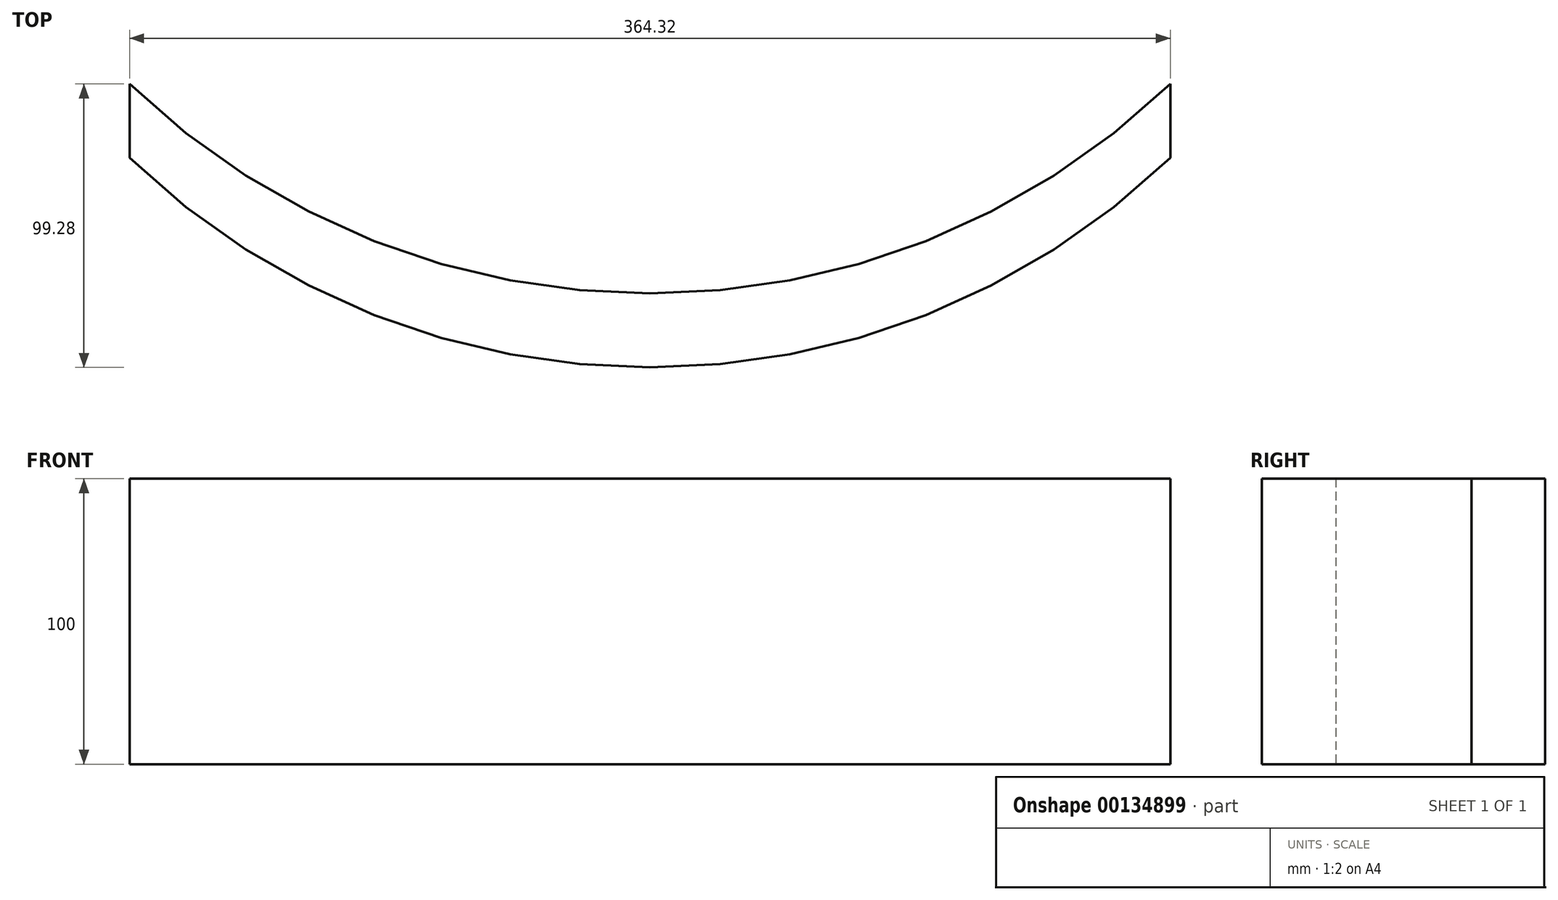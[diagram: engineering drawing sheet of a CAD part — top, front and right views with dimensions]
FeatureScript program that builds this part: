
annotation { "Feature Type Name" : "Feature", "Feature Type Description" : "" }
export const myFeature = defineFeature(function(context is Context, id is Id, definition is map)
    precondition{}
    {
        {
            var Q0;
            Q0=qCreatedBy(makeId("Top.planeOp"),FACE);
            var sketch = newSketch(context, id + "F0", { "sketchPlane" : qUnion([Q0])});
            skArc(sketch, "E0", {"start": v(-182.16, -189.43) * mm, "mid": v(0, -262.8) * mm, "end": v(182.16, -189.43) * mm});
            skLineSegment(sketch, "E1", {"start": v(-182.16, -189.43) * mm, "end": v(182.16, -189.43) * mm, "construction": true});
            skSolve(sketch);
        }
        {
            var Q0;
            Q0 = qSketchRegion(id + "F0", true);
            var Q1;
            Q1=sQuery(id+"F0.wireOp",EDGE,"E0");
            extrude(context, id + "F1", {"entities" : qUnion([Q0]), "bodyType" : ToolBodyType.SURFACE, "surfaceEntities" : qUnion([Q1]), "oppositeDirection" : true, "depth" : 100 * mm});
        }
        {
            var Q0;
            Q0=makeQuery(id+"F1.opExtrude","SWEPT_BODY",BODY,{"disambiguationData":[OSD([sQuery(id+"F0.wireOp",EDGE,"E0")])]});
            transform(context, id + "F2", {"entities" : qUnion([Q0]), "transformType" : TransformType.TRANSLATION_3D, "dx" : 0 * mm, "dy" : -25.9 * mm, "dz" : 0 * mm, "makeCopy" : true});
        }
        {
            var Q0;
            Q0=makeQuery(id+"F1.opExtrude","SWEPT_FACE",FACE,{"disambiguationData":[OSD([sQuery(id+"F0.wireOp",EDGE,"E0")])]});
            var Q1;
            Q1=makeQuery(id+"F2.opPattern","COPY",FACE,{"derivedFrom":makeQuery(id+"F1.opExtrude","SWEPT_FACE",FACE,{"disambiguationData":[OSD([sQuery(id+"F0.wireOp",EDGE,"E0")])]}),"instanceName":"1"});
            loft(context, id + "F3", {"sheetProfilesArray" : [{ "sheetProfileEntities" : qUnion([Q0]) }, { "sheetProfileEntities" : qUnion([Q1]) }]});
        }
    });
